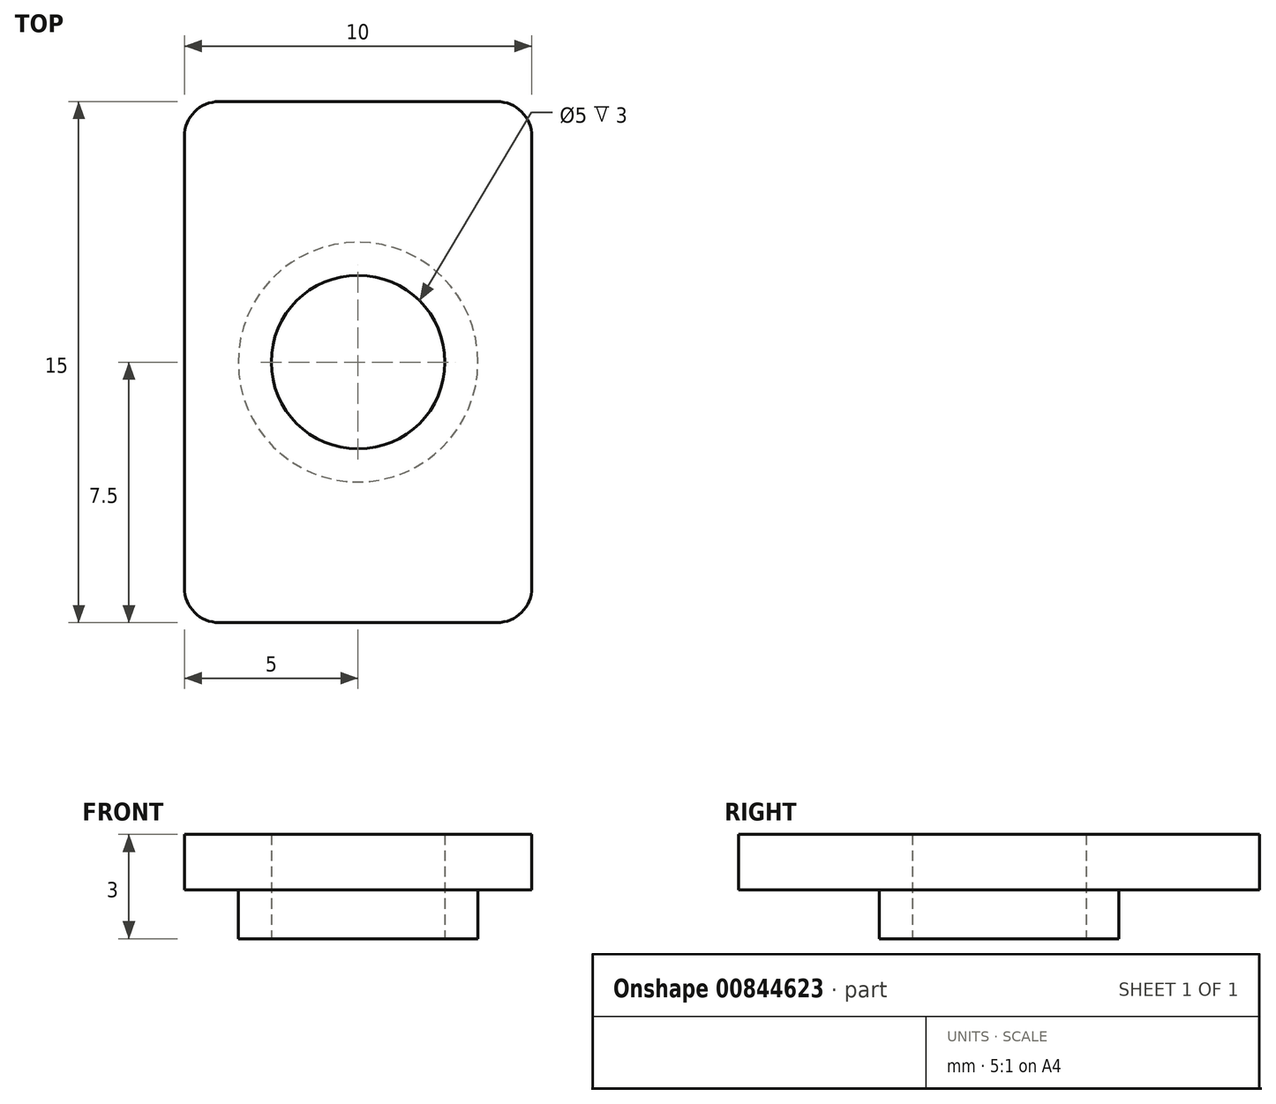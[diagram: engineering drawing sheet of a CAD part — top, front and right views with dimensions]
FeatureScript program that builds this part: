
annotation { "Feature Type Name" : "Feature", "Feature Type Description" : "" }
export const myFeature = defineFeature(function(context is Context, id is Id, definition is map)
    precondition{}
    {
        {
            var Q0;
            Q0=qCreatedBy(makeId("Top.planeOp"),FACE);
            var sketch = newSketch(context, id + "F0", { "sketchPlane" : qUnion([Q0])});
            skLineSegment(sketch, "E0.bottom", {"start": v(4, -7.5) * mm, "end": v(-4, -7.5) * mm});
            skLineSegment(sketch, "E0.top", {"start": v(4, 7.5) * mm, "end": v(-4, 7.5) * mm});
            skLineSegment(sketch, "E0.left", {"start": v(5, -6.5) * mm, "end": v(5, 6.5) * mm});
            skLineSegment(sketch, "E0.right", {"start": v(-5, -6.5) * mm, "end": v(-5, 6.5) * mm});
            skPoint(sketch, "E0.middle", {"position": v(0, 0) * mm});
            skCircle(sketch, "E1", {"center": v(0, 0) * mm, "radius": 2.5 * mm});
            skPoint(sketch, "E2.visualSharp", {"position": v(-5, 7.5) * mm});
            skArc(sketch, "E2.filletArc", {"start": v(-4, 7.5) * mm, "mid": v(-4.7, 7.2) * mm, "end": v(-5, 6.5) * mm});
            skPoint(sketch, "E3.visualSharp", {"position": v(5, 7.5) * mm});
            skArc(sketch, "E3.filletArc", {"start": v(5, 6.5) * mm, "mid": v(4.7, 7.2) * mm, "end": v(4, 7.5) * mm});
            skPoint(sketch, "E4.visualSharp", {"position": v(5, -7.5) * mm});
            skArc(sketch, "E4.filletArc", {"start": v(4, -7.5) * mm, "mid": v(4.7, -7.2) * mm, "end": v(5, -6.5) * mm});
            skPoint(sketch, "E5.visualSharp", {"position": v(-5, -7.5) * mm});
            skArc(sketch, "E5.filletArc", {"start": v(-5, -6.5) * mm, "mid": v(-4.7, -7.2) * mm, "end": v(-4, -7.5) * mm});
            skSolve(sketch);
        }
        {
            var Q0;
            Q0 = qSketchRegion(id + "F0", true);
            extrude(context, id + "F1", {"entities" : qUnion([Q0]), "depth" : 1.6 * mm, "offsetDistance" : 25 * mm});
        }
        {
            var Q0;
            Q0=qCreatedBy(makeId("Top.planeOp"),FACE);
            var sketch = newSketch(context, id + "F2", { "sketchPlane" : qUnion([Q0])});
            skCircle(sketch, "E6.0", {"center": v(0, 0) * mm, "radius": 2.5 * mm});
            skCircle(sketch, "E7", {"center": v(0, 0) * mm, "radius": 3.45 * mm});
            skSolve(sketch);
        }
        {
            var Q0;
            Q0 = qSketchRegion(id + "F2", true);
            extrude(context, id + "F3", {"entities" : qUnion([Q0]), "operationType" : NewBodyOperationType.ADD, "oppositeDirection" : true, "depth" : (3 - 1.6) * mm, "offsetDistance" : 25 * mm});
        }
    });
